FREECAD ASSEMBLY — COMPONENT RECIPES ("assembly")

This assembly document has 4 components, labeled P0..P3 below (a component is one placed body or linked part). 0 of them carry a construction recipe — the FreeCAD feature program that regenerates the part from scratch, quoted from this document or its linked companion documents; the rest are supplied as boundary geometry only. No exploded tour is included for this assembly.
COMPONENT P0 — geometry summary ("laptop_body"; no construction recipe available for this part):
  bounding box: 330.0 x 282.7 x 213.4 mm
  tessellated surface: 20 triangles
  volume: 1547082 mm^3 (8% of its bounding box)
  symmetry: mirror-symmetric across its x mid-plane
COMPONENT P1 — geometry summary ("riser_body_left"; no construction recipe available for this part):
  bounding box: 20.8 x 11.0 x 10.0 mm
  tessellated surface: 2,212 triangles
  volume: 1717 mm^3 (75% of its bounding box)
  symmetry: mirror-symmetric across its x mid-plane
COMPONENT P2 — geometry summary ("riser_body_right"; no construction recipe available for this part):
  bounding box: 20.8 x 11.0 x 10.0 mm
  tessellated surface: 2,212 triangles
  volume: 1717 mm^3 (75% of its bounding box)
  symmetry: mirror-symmetric across its x mid-plane
COMPONENT P3 — geometry summary ("table_body"; no construction recipe available for this part):
  bounding box: 500.0 x 300.0 x 10.0 mm
  tessellated surface: 12 triangles
  volume: 1500000 mm^3 (100% of its bounding box)
  symmetry: 2-fold rotationally symmetric about the x axis; 2-fold rotationally symmetric about the y axis; 2-fold rotationally symmetric about the z axis; mirror-symmetric across its x mid-plane, y mid-plane, z mid-plane
PROVENANCE & LICENSES
A FreeCAD (.FCStd) document from a public repository crawl; recipes are the document's own serialized feature recipes (and, for linked parts, companion documents' recipes).
License: other.
